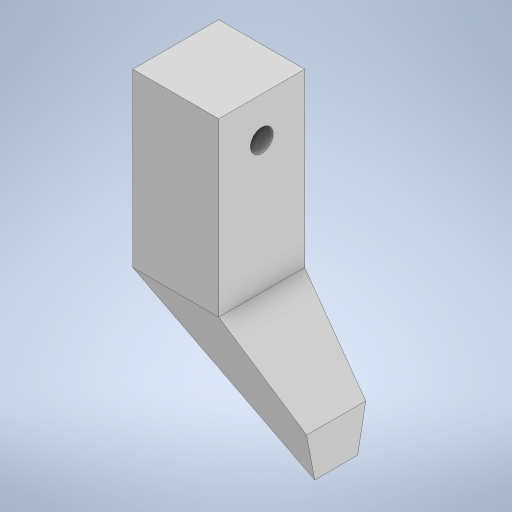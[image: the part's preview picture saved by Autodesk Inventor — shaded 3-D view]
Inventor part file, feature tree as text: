
AUTODESK INVENTOR PART (.ipt)
format: ipt  version: 2024 (Build 280153000, 153)  size: 235,008 bytes
history: native  units: in
note: dims shown in document units (in); Inventor stores cm internally (conversion verified against a paired STEP export)
features: extrude x3, sketch x3
ambient origin geometry x8: Origin, YZ Plane, XZ Plane, XY Plane, X Axis, Y Axis, Z Axis, Center Point
bodies: Solid1 (feature_tree)
feature tree (6):
  extrude  "Extrusion1"  Depth=1.5in
  extrude  "Extrusion2"  Depth=2.8in
  extrude  "Extrusion3"  Depth=1.5in TaperAngle=0.0deg
  sketch  "Sketch1"  dims[d0=3.0in d1=1.5in]
  sketch  "Sketch3"  dims[d3=2.8in d4=2.0in]
  sketch  "Sketch4"  dims[d5=0.75in d6=1.5in d7=0.0in d9=0.375in d10=1.5in d11=0.0in d12=1.3in d13=0.3976in d14=0.7in d15=1.0in d16=0.0in]
